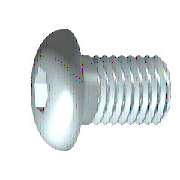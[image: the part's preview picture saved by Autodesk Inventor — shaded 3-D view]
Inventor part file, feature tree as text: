
AUTODESK INVENTOR PART (.ipt)
format: ipt  version: 2023.5 (Build 275446000, 446)  size: 192,512 bytes
history: native  units: mm (DEFAULTED — no unit token found)
features: extrude x1, plane x1, fillet x1
ambient origin geometry x7: Origin, YZ Plane, XY Plane, X Axis, Y Axis, Z Axis, Center Point
bodies: Solid1 (feature_tree), Body (feature_tree)
feature tree (3):
  extrude  "Slot"  Depth=11.1758mm
  plane  "Work Plane1"
  fillet  "Fillet2"  Radius=1.5241mm
